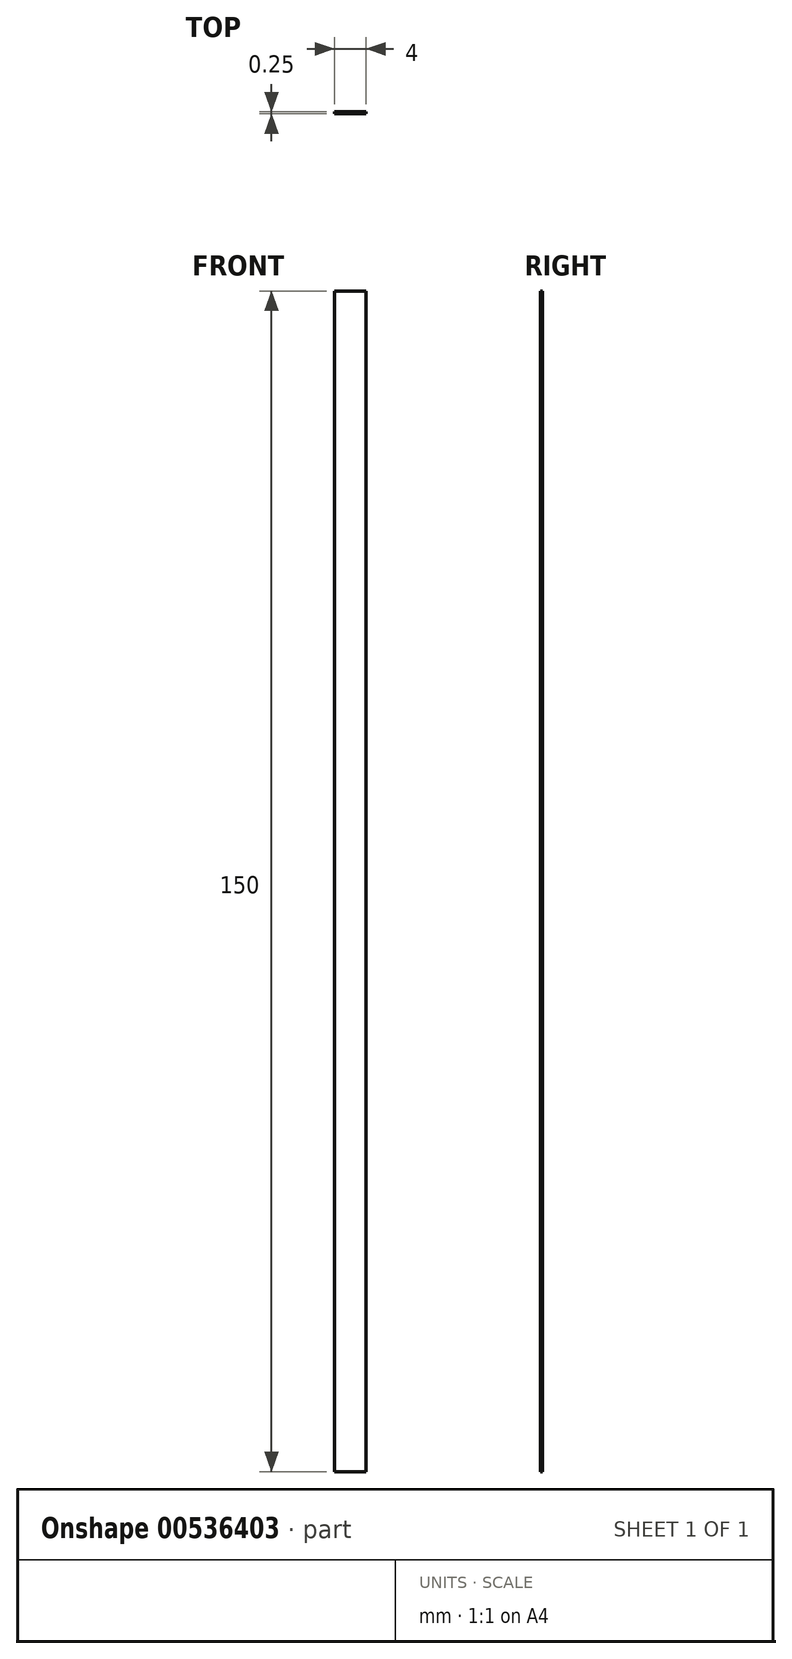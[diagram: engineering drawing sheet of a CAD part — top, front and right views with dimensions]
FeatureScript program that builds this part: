
annotation { "Feature Type Name" : "Feature", "Feature Type Description" : "" }
export const myFeature = defineFeature(function(context is Context, id is Id, definition is map)
    precondition{}
    {
        {
            var Q0;
            Q0=qCreatedBy(makeId("Front.planeOp"),FACE);
            var sketch = newSketch(context, id + "F0", { "sketchPlane" : qUnion([Q0])});
            skLineSegment(sketch, "E0.bottom", {"start": v(2.07, -75) * mm, "end": v(-1.93, -75) * mm});
            skLineSegment(sketch, "E0.top", {"start": v(2.07, 75) * mm, "end": v(-1.93, 75) * mm});
            skLineSegment(sketch, "E0.left", {"start": v(2.07, -75) * mm, "end": v(2.07, 75) * mm});
            skLineSegment(sketch, "E0.right", {"start": v(-1.93, -75) * mm, "end": v(-1.93, 75) * mm});
            skPoint(sketch, "E0.middle", {"position": v(0.07, 0) * mm});
            skSolve(sketch);
        }
        {
            var Q0;
            Q0=makeQuery(id+"F0.imprint","IMPRINT",FACE,{"disambiguationData":[TD([[makeQuery(id+"F0.imprint","IMPRINT",EDGE,{"derivedFrom":sQuery(id+"F0.wireOp",EDGE,"E0.bottom")}),-1.0]])]});
            extrude(context, id + "F1", {"entities" : qUnion([Q0]), "depth" : 0.25 * mm});
        }
    });
